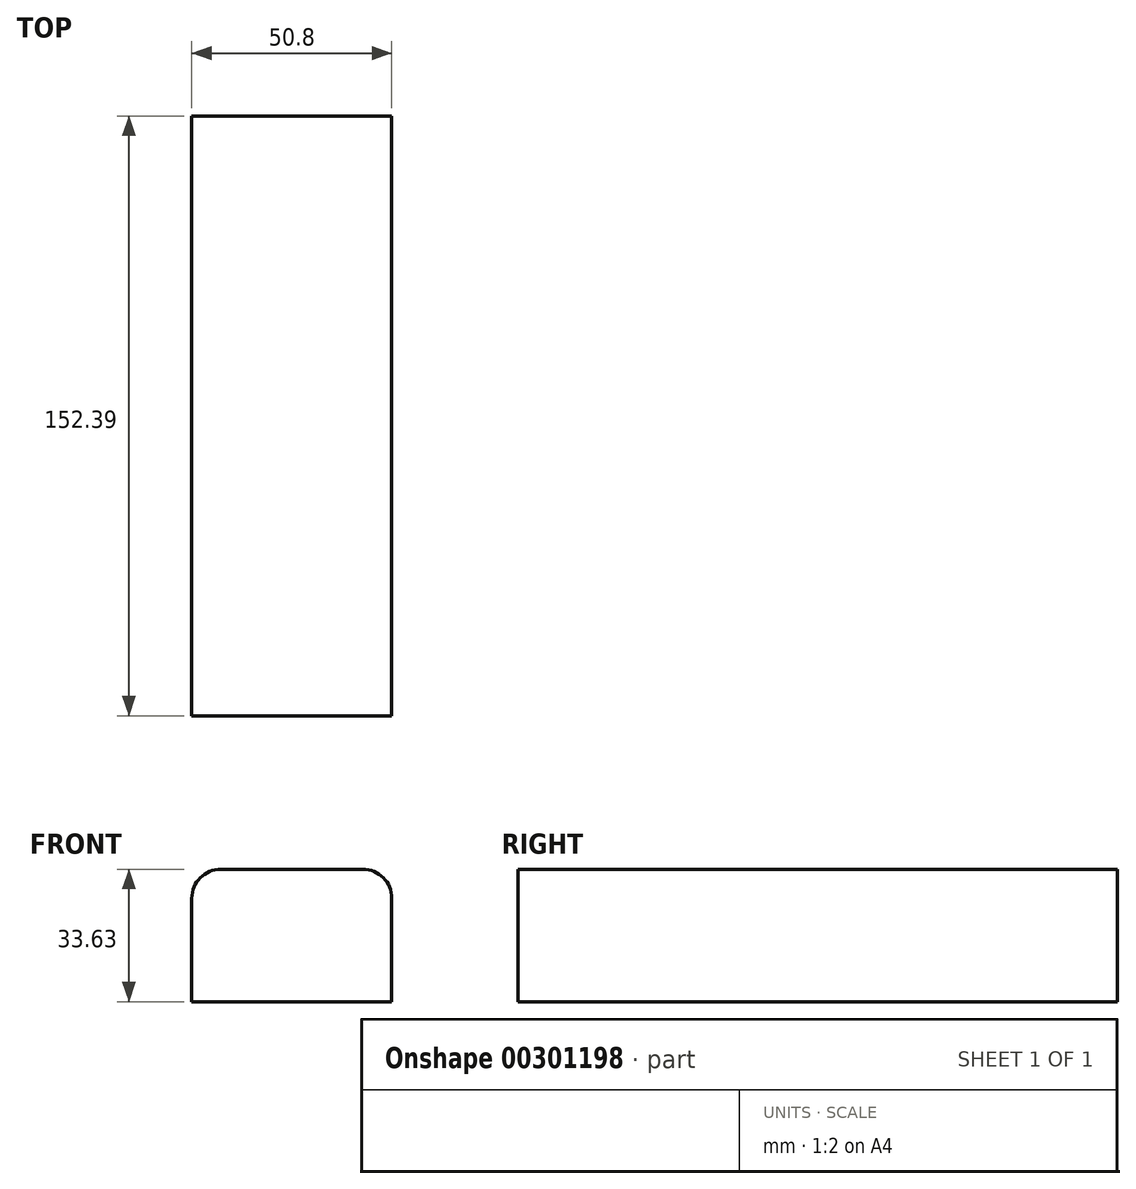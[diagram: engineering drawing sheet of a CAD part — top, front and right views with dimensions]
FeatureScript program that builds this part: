
annotation { "Feature Type Name" : "Feature", "Feature Type Description" : "" }
export const myFeature = defineFeature(function(context is Context, id is Id, definition is map)
    precondition{}
    {
        {
            var Q0;
            Q0=qCreatedBy(makeId("Right.planeOp"),FACE);
            var sketch = newSketch(context, id + "F0", { "sketchPlane" : qUnion([Q0])});
            skLineSegment(sketch, "E0", {"start": v(-82.9, 29.41) * mm, "end": v(-82.9, -4.22) * mm});
            skLineSegment(sketch, "E1.bottom", {"start": v(-82.9, 29.41) * mm, "end": v(69.5, 29.41) * mm});
            skLineSegment(sketch, "E1.top", {"start": v(-82.9, -4.22) * mm, "end": v(69.5, -4.22) * mm});
            skLineSegment(sketch, "E1.right", {"start": v(69.5, 29.41) * mm, "end": v(69.5, -4.22) * mm});
            skSolve(sketch);
        }
        {
            var Q0;
            Q0=makeQuery(id+"F0.imprint","IMPRINT",FACE,{"disambiguationData":[TD([[makeQuery(id+"F0.imprint","IMPRINT",EDGE,{"derivedFrom":sQuery(id+"F0.wireOp",EDGE,"E1.bottom")}),-1.0]])]});
            extrude(context, id + "F1", {"entities" : qUnion([Q0]), "depth" : 50.8 * mm});
        }
        {
            var Q0;
            Q0=makeQuery(id+"F1.opExtrude","CAP_EDGE",EDGE,{"disambiguationData":[OSD([sQuery(id+"F0.wireOp",EDGE,"E1.bottom")])],"isStart":false});
            var Q1;
            Q1=makeQuery(id+"F1.opExtrude","CAP_EDGE",EDGE,{"disambiguationData":[OSD([sQuery(id+"F0.wireOp",EDGE,"E1.bottom")])],"isStart":true});
            fillet(context, id + "F2", {"entities" : qUnion([Q0, Q1]), "radius" : 7.36 * mm, "tangentPropagation" : true, "allowEdgeOverflow" : false});
        }
    });
